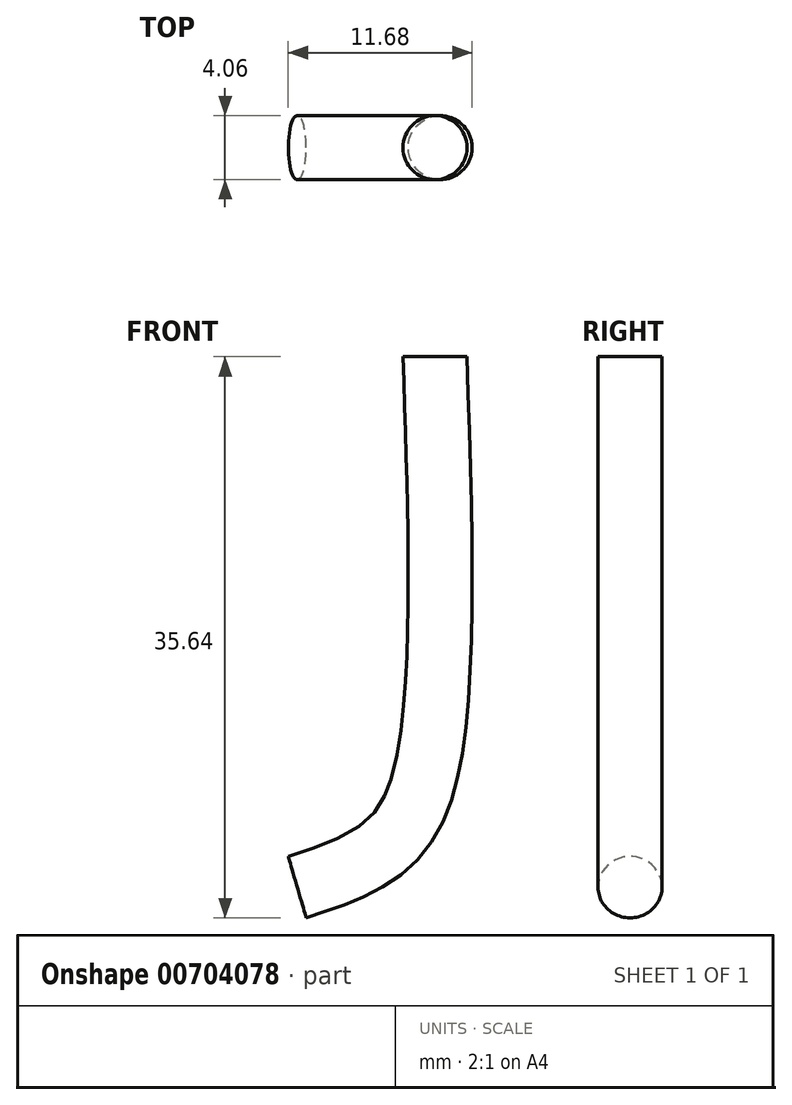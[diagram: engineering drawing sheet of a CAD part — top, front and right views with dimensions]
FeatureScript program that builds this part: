
annotation { "Feature Type Name" : "Feature", "Feature Type Description" : "" }
export const myFeature = defineFeature(function(context is Context, id is Id, definition is map)
    precondition{}
    {
        {
            var Q0;
            Q0=qCreatedBy(makeId("Front.planeOp"),FACE);
            var sketch = newSketch(context, id + "F0", { "sketchPlane" : qUnion([Q0])});
            skFitSpline(sketch, "E0", {"points": [v(0, 0) * mm, v(0, -22.74) * mm, v(-2.66, -30.65) * mm, v(-8.75, -33.7) * mm], "startDerivative": vector(1.85, -54.4) * mm, "endDerivative": vector(-27.12, -8.93) * mm});
            skSolve(sketch);
        }
        {
            var Q0;
            Q0=qCreatedBy(makeId("Top.planeOp"),FACE);
            var sketch = newSketch(context, id + "F1", { "sketchPlane" : qUnion([Q0])});
            skCircle(sketch, "E1", {"center": v(0, 0) * mm, "radius": 2.03 * mm});
            skSolve(sketch);
        }
        {
            var Q0;
            Q0=makeQuery(id+"F1.imprint","IMPRINT",FACE,{"disambiguationData":[TD([[makeQuery(id+"F1.imprint","IMPRINT",EDGE,{"derivedFrom":sQuery(id+"F1.wireOp",EDGE,"E1")}),1.0]])]});
            var Q1;
            Q1=sQuery(id+"F0.wireOp",EDGE,"E0");
            sweep(context, id + "F2", {"profiles" : qUnion([Q0]), "path" : qUnion([Q1])});
        }
    });
